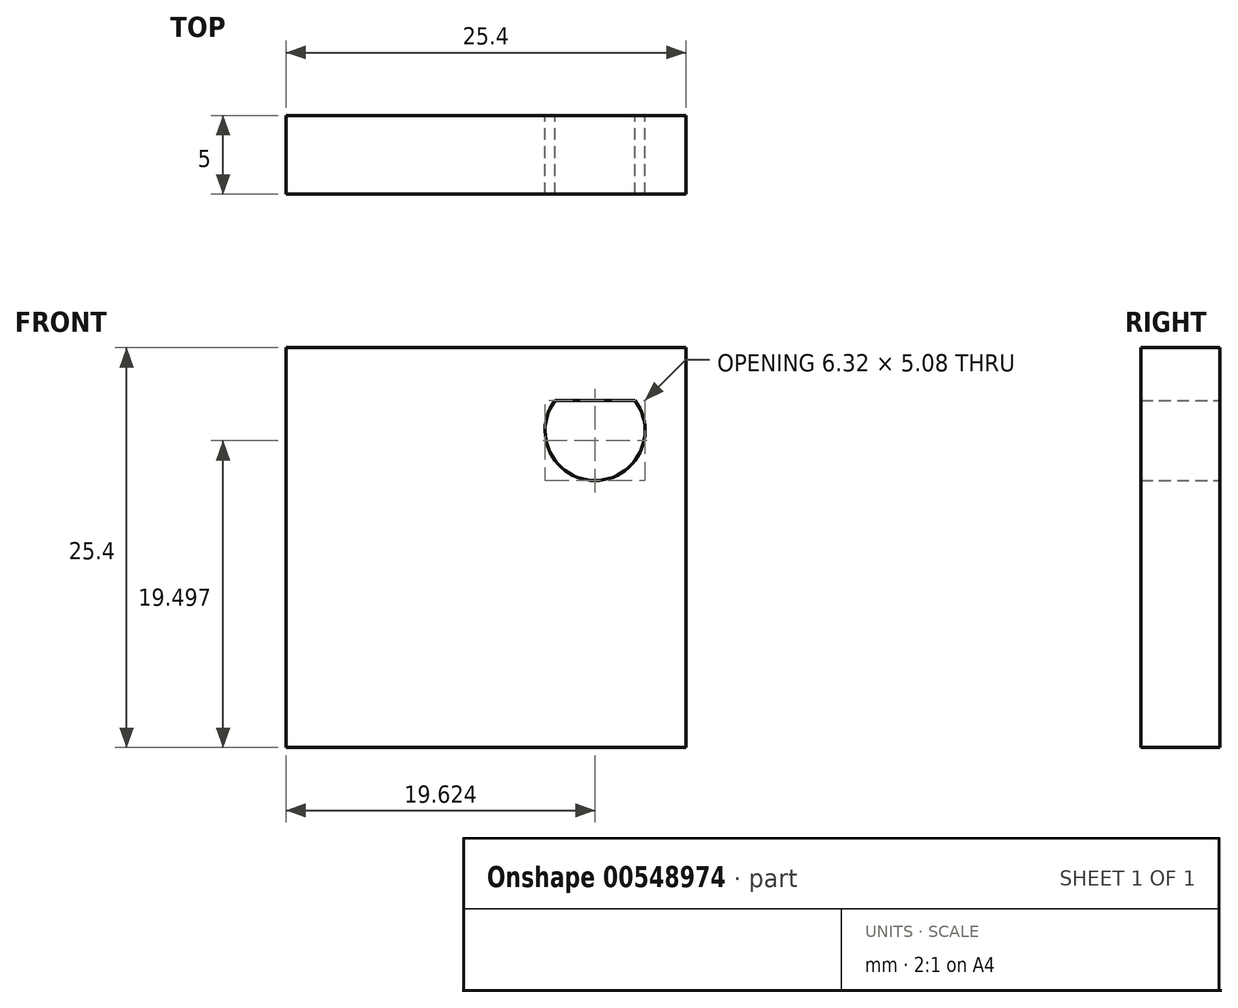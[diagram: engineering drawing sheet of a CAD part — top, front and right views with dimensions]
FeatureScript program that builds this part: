
annotation { "Feature Type Name" : "Feature", "Feature Type Description" : "" }
export const myFeature = defineFeature(function(context is Context, id is Id, definition is map)
    precondition{}
    {
        {
            var Q0;
            Q0=qCreatedBy(makeId("Front.planeOp"),FACE);
            var sketch = newSketch(context, id + "F0", { "sketchPlane" : qUnion([Q0])});
            skLineSegment(sketch, "E0.bottom", {"start": v(33.41, 41.96) * mm, "end": v(58.81, 41.96) * mm});
            skLineSegment(sketch, "E0.top", {"start": v(33.41, 67.36) * mm, "end": v(58.81, 67.36) * mm});
            skLineSegment(sketch, "E0.left", {"start": v(33.41, 41.96) * mm, "end": v(33.41, 67.36) * mm});
            skLineSegment(sketch, "E0.right", {"start": v(58.81, 41.96) * mm, "end": v(58.81, 67.36) * mm});
            skCircle(sketch, "E1", {"center": v(53.03, 62.1) * mm, "radius": 3.18 * mm});
            skLineSegment(sketch, "E2", {"start": v(50.5, 64) * mm, "end": v(55.57, 64) * mm});
            skSolve(sketch);
        }
        {
            var Q0;
            Q0=makeQuery(id+"F0.imprint","IMPRINT",FACE,{"disambiguationData":[TD([[makeQuery(id+"F0.imprint","IMPRINT",EDGE,{"derivedFrom":sQuery(id+"F0.wireOp",EDGE,"E0.bottom")}),1.0]])]});
            var Q1;
            {var subQ0=sQuery(id+"F0.wireOp",EDGE,"E2");Q1=makeQuery(id+"F0.imprint","IMPRINT",FACE,{"disambiguationData":[TD([[makeQuery(id+"F0.imprint","IMPRINT",EDGE,{"derivedFrom":subQ0}),1.0]])]});}
            extrude(context, id + "F1", {"entities" : qUnion([Q0, Q1]), "depth" : 5 * mm, "offsetDistance" : 25.4 * mm});
        }
    });
